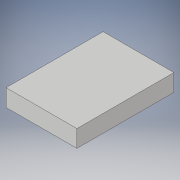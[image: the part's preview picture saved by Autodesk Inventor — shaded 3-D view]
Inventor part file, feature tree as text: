
AUTODESK INVENTOR PART (.ipt)
format: ipt  version: 2017 (Build 210142000, 142)  size: 87,552 bytes
history: native  units: in
note: dims shown in document units (in); Inventor stores cm internally (conversion verified against a paired STEP export)
features: extrude x1, sketch x1
ambient origin geometry x8: Origin, YZ Plane, XZ Plane, XY Plane, X Axis, Y Axis, Z Axis, Center Point
bodies: Solid1 (feature_tree)
feature tree (2):
  extrude  "Extrusion1"  Depth=5.8in
  sketch  "Sketch1"  dims[d0=4.235in d1=5.8in d2=1.025in d3=0.0in]
